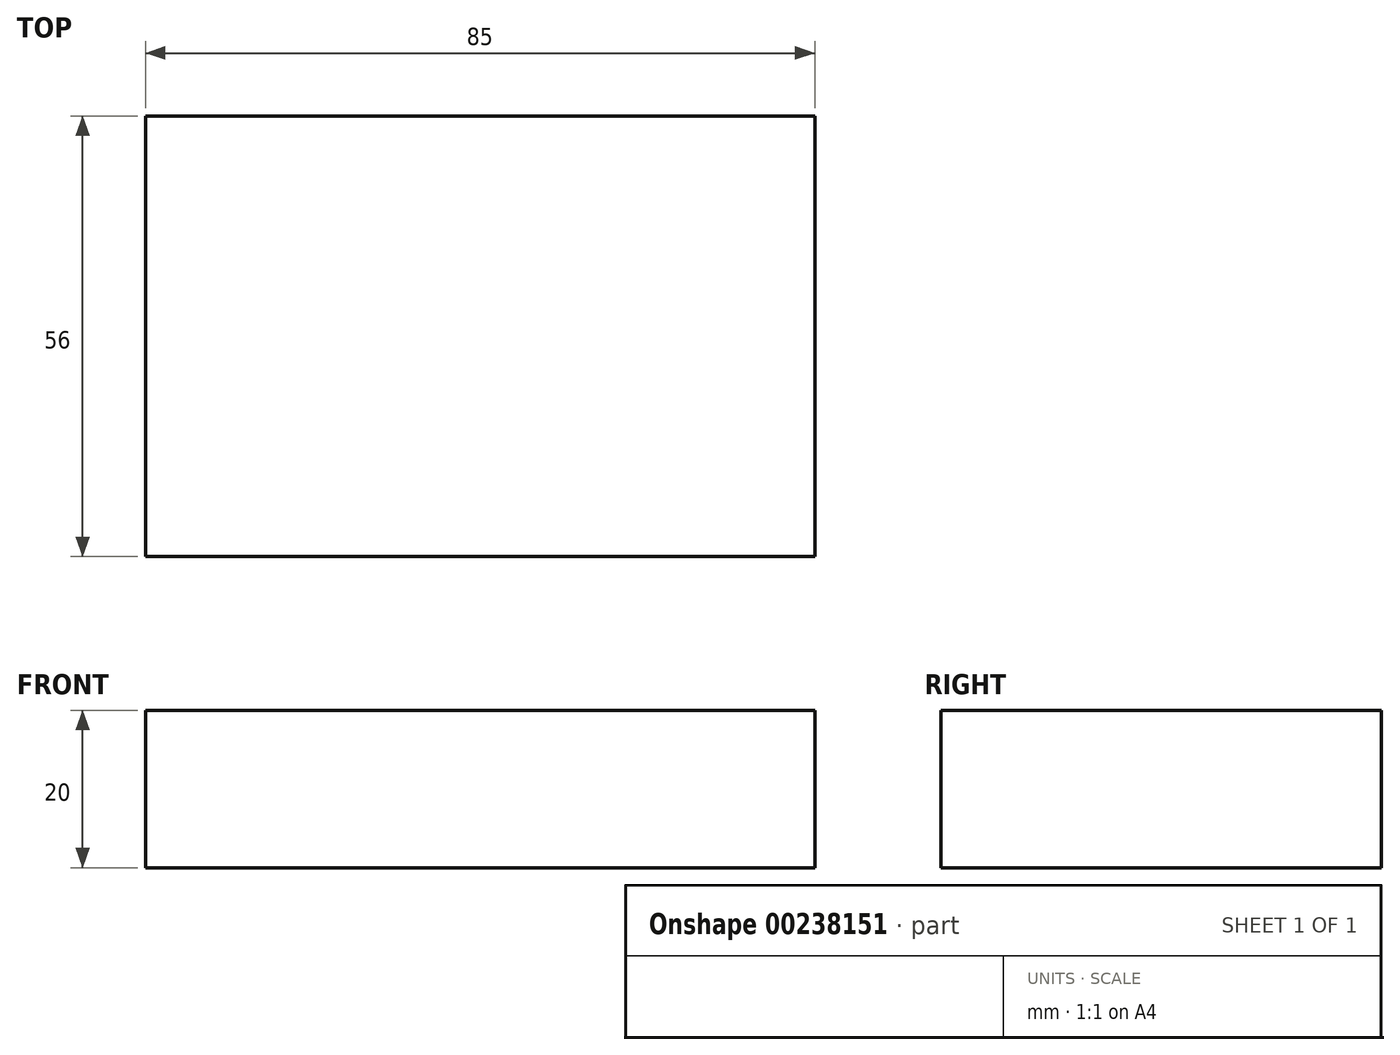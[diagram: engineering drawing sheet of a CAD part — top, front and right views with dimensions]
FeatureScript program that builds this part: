
annotation { "Feature Type Name" : "Feature", "Feature Type Description" : "" }
export const myFeature = defineFeature(function(context is Context, id is Id, definition is map)
    precondition{}
    {
        {
            var Q0;
            Q0=qCreatedBy(makeId("Top.planeOp"),FACE);
            var sketch = newSketch(context, id + "F0", { "sketchPlane" : qUnion([Q0])});
            skLineSegment(sketch, "E0.bottom", {"start": v(-42.5, 28) * mm, "end": v(42.5, 28) * mm});
            skLineSegment(sketch, "E0.top", {"start": v(-42.5, -28) * mm, "end": v(42.5, -28) * mm});
            skLineSegment(sketch, "E0.left", {"start": v(-42.5, 28) * mm, "end": v(-42.5, -28) * mm});
            skLineSegment(sketch, "E0.right", {"start": v(42.5, 28) * mm, "end": v(42.5, -28) * mm});
            skPoint(sketch, "E0.middle", {"position": v(0, 0) * mm});
            skSolve(sketch);
        }
        {
            var Q0;
            Q0=makeQuery(id+"F0.imprint","IMPRINT",FACE,{"disambiguationData":[TD([[makeQuery(id+"F0.imprint","IMPRINT",EDGE,{"derivedFrom":sQuery(id+"F0.wireOp",EDGE,"E0.bottom")}),-1.0]])]});
            extrude(context, id + "F1", {"entities" : qUnion([Q0]), "oppositeDirection" : true, "depth" : 20 * mm});
        }
    });
